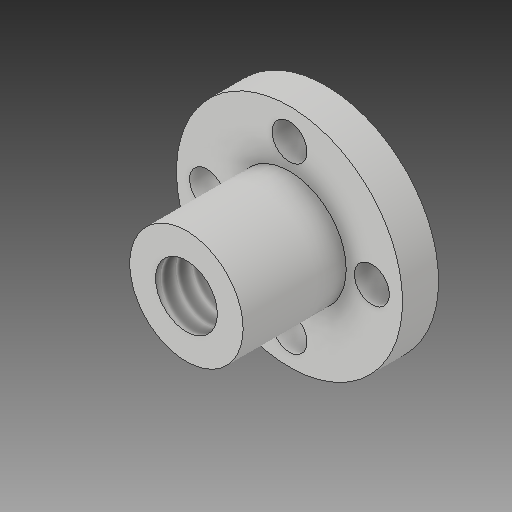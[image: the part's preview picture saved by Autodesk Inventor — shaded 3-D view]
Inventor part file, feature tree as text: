
AUTODESK INVENTOR PART (.ipt)
format: ipt  version: 2017 (Build 210142000, 142)  size: 150,528 bytes
history: native  units: mm
features: reference x5, extrude x3, sketch x3, other x3, thread x1
ambient origin geometry x8: Origin, YZ Plane, XZ Plane, XY Plane, X Axis, Y Axis, Z Axis, Center Point
bodies: Solid1 (feature_tree)
feature tree (15):
  extrude  "Extrusion1"  Depth=10.16mm
  extrude  "Extrusion2"  Depth=3.5mm
  extrude  "Extrusion3"  Depth=10.0mm TaperAngle=0.0deg
  thread  "Thread1"  [1 undecoded]
  sketch  "Sketch1"  dims[d0=21.93mm d1=10.16mm]
  reference  "Reference1"
  sketch  "Sketch2"  dims[d2=3.5mm d3=0.0mm d4=6.0mm]
  sketch  "Sketch3"  dims[d5=10.0mm d6=0.0mm d7=10.0mm d8=0.0mm d9=10.0mm d10=0.0mm]
  reference  "Reference2"
  reference  "Reference3"
  reference  "Reference4"
  reference  "Reference5"
  parser-record x1  (decoder bookkeeping rows leaked as tree rows — omitted from the tree; the rows remain in map.json)
  other  "Front-Bed-Holder.iam"
  other  "Left Bed Holder Mid:1"
note: 1 required parameter value undecoded (feature->parameter linkage not recoverable at this tier; creation-order binding heuristic only, values carry confidence <= 0.55)
note: 1 file-system path scrubbed to <path> (originals preserved in map.json)
